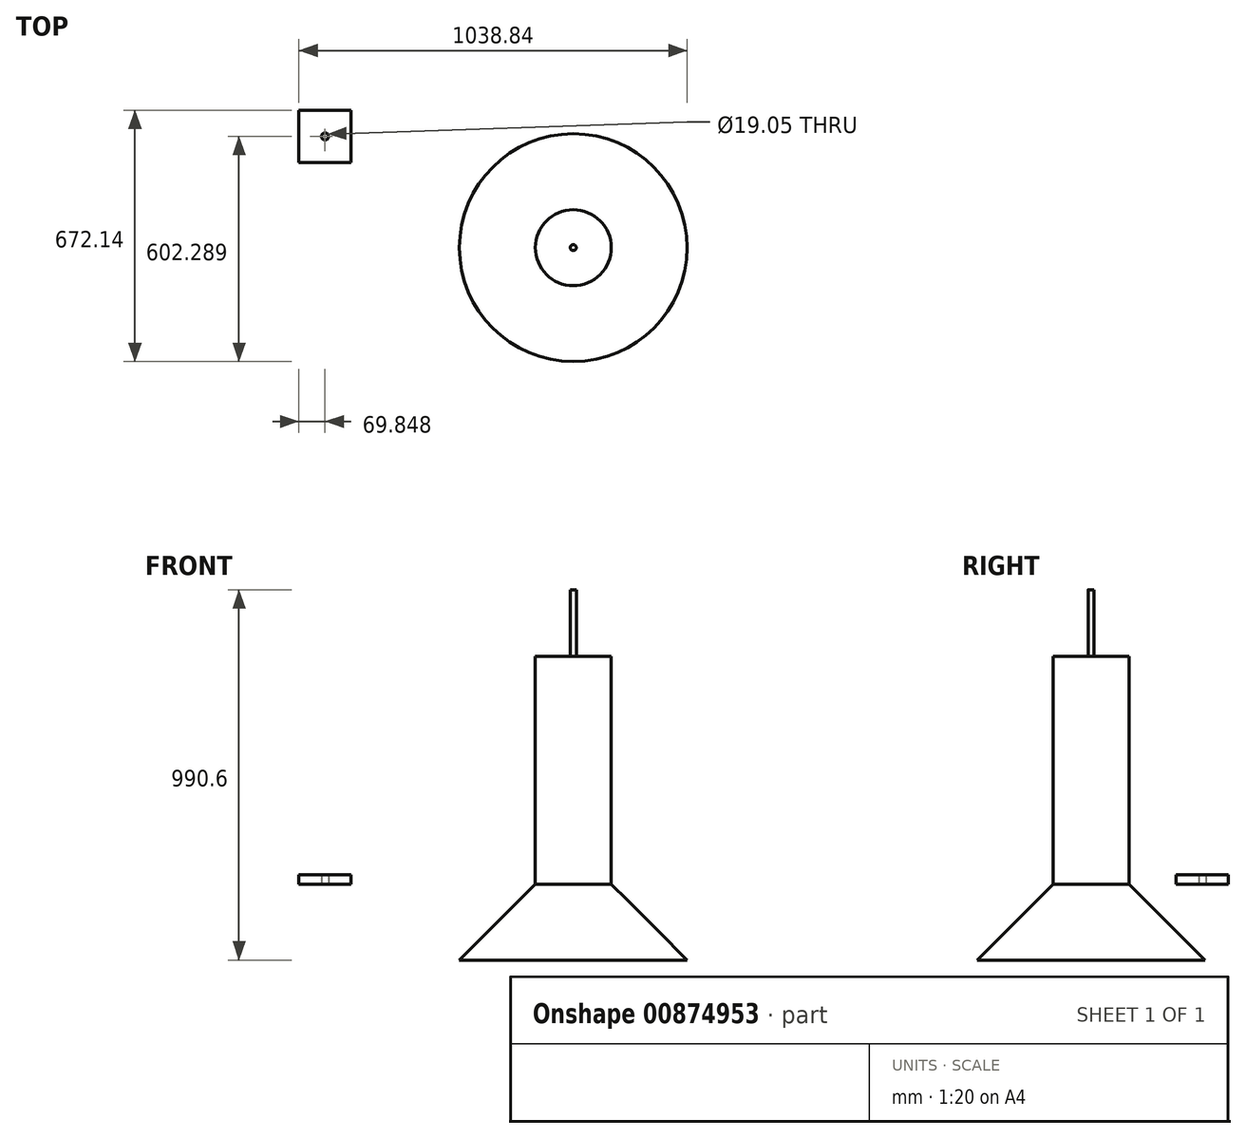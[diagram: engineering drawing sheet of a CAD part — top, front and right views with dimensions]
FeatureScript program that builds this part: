
annotation { "Feature Type Name" : "Feature", "Feature Type Description" : "" }
export const myFeature = defineFeature(function(context is Context, id is Id, definition is map)
    precondition{}
    {
        {
            var Q0;
            Q0=qCreatedBy(makeId("Top.planeOp"),FACE);
            var sketch = newSketch(context, id + "F0", { "sketchPlane" : qUnion([Q0])});
            skCircle(sketch, "E0", {"center": v(0, 0) * mm, "radius": 101.6 * mm});
            skSolve(sketch);
        }
        {
            var Q0;
            Q0=makeQuery(id+"F0.imprint","IMPRINT",FACE,{"disambiguationData":[TD([[makeQuery(id+"F0.imprint","IMPRINT",EDGE,{"derivedFrom":sQuery(id+"F0.wireOp",EDGE,"E0")}),1.0]])]});
            extrude(context, id + "F1", {"entities" : qUnion([Q0]), "depth" : 609.6 * mm, "offsetDistance" : 25.4 * mm});
        }
        {
            var Q0;
            Q0=qCreatedBy(makeId("Top.planeOp"),FACE);
            cPlane(context, id + "F2", {"entities" : qUnion([Q0]), "cplaneType" : CPlaneType.OFFSET, "offset" : 203.2 * mm, "oppositeDirection" : true, "width" : 152.4 * mm, "height" : 152.4 * mm});
        }
        {
            var Q0;
            Q0=qCreatedBy(id+"F2.planeOp",FACE);
            var sketch = newSketch(context, id + "F3", { "sketchPlane" : qUnion([Q0])});
            skCircle(sketch, "E1", {"center": v(0, 0) * mm, "radius": 304.8 * mm});
            skSolve(sketch);
        }
        {
            var Q1;
            Q1=makeQuery(id+"F3.imprint","IMPRINT",FACE,{"disambiguationData":[TD([[makeQuery(id+"F3.imprint","IMPRINT",EDGE,{"derivedFrom":sQuery(id+"F3.wireOp",EDGE,"E1")}),1.0]])]});
            var Q2;
            Q2=makeQuery(id+"F1.opExtrude","CAP_FACE",FACE,{"disambiguationData":[OSD([sQuery(id+"F0.wireOp",EDGE,"E0")])],"isStart":true});
            loft(context, id + "F4", {"operationType" : NewBodyOperationType.ADD, "sheetProfilesArray" : [{ "sheetProfileEntities" : qUnion([Q1]) }, { "sheetProfileEntities" : qUnion([Q2]) }]});
        }
        {
            var Q0;
            Q0=makeQuery(id+"F1.opExtrude","CAP_FACE",FACE,{"disambiguationData":[OSD([sQuery(id+"F0.wireOp",EDGE,"E0")])],"isStart":false});
            var sketch = newSketch(context, id + "F5", { "sketchPlane" : qUnion([Q0])});
            skCircle(sketch, "E2", {"center": v(0, 0) * mm, "radius": 7.94 * mm});
            skSolve(sketch);
        }
        {
            var Q0;
            Q0 = qSketchRegion(id + "F5", true);
            extrude(context, id + "F6", {"entities" : qUnion([Q0]), "operationType" : NewBodyOperationType.ADD, "depth" : 177.8 * mm, "offsetDistance" : 25.4 * mm});
        }
        {
            var Q0;
            Q0=qCreatedBy(makeId("Top.planeOp"),FACE);
            var sketch = newSketch(context, id + "F7", { "sketchPlane" : qUnion([Q0])});
            skLineSegment(sketch, "E3.bottom", {"start": v(-734.04, 367.34) * mm, "end": v(-594.34, 367.34) * mm});
            skLineSegment(sketch, "E3.top", {"start": v(-734.04, 227.64) * mm, "end": v(-594.34, 227.64) * mm});
            skLineSegment(sketch, "E3.left", {"start": v(-734.04, 367.34) * mm, "end": v(-734.04, 227.64) * mm});
            skLineSegment(sketch, "E3.right", {"start": v(-594.34, 367.34) * mm, "end": v(-594.34, 227.64) * mm});
            skCircle(sketch, "E4", {"center": v(-664.2, 297.49) * mm, "radius": 9.53 * mm});
            skSolve(sketch);
        }
        {
            var Q0;
            Q0=makeQuery(id+"F7.imprint","IMPRINT",FACE,{"disambiguationData":[TD([[makeQuery(id+"F7.imprint","IMPRINT",EDGE,{"derivedFrom":sQuery(id+"F7.wireOp",EDGE,"E3.bottom")}),-1.0]])]});
            extrude(context, id + "F8", {"entities" : qUnion([Q0]), "depth" : 25.4 * mm, "offsetDistance" : 25.4 * mm});
        }
    });
